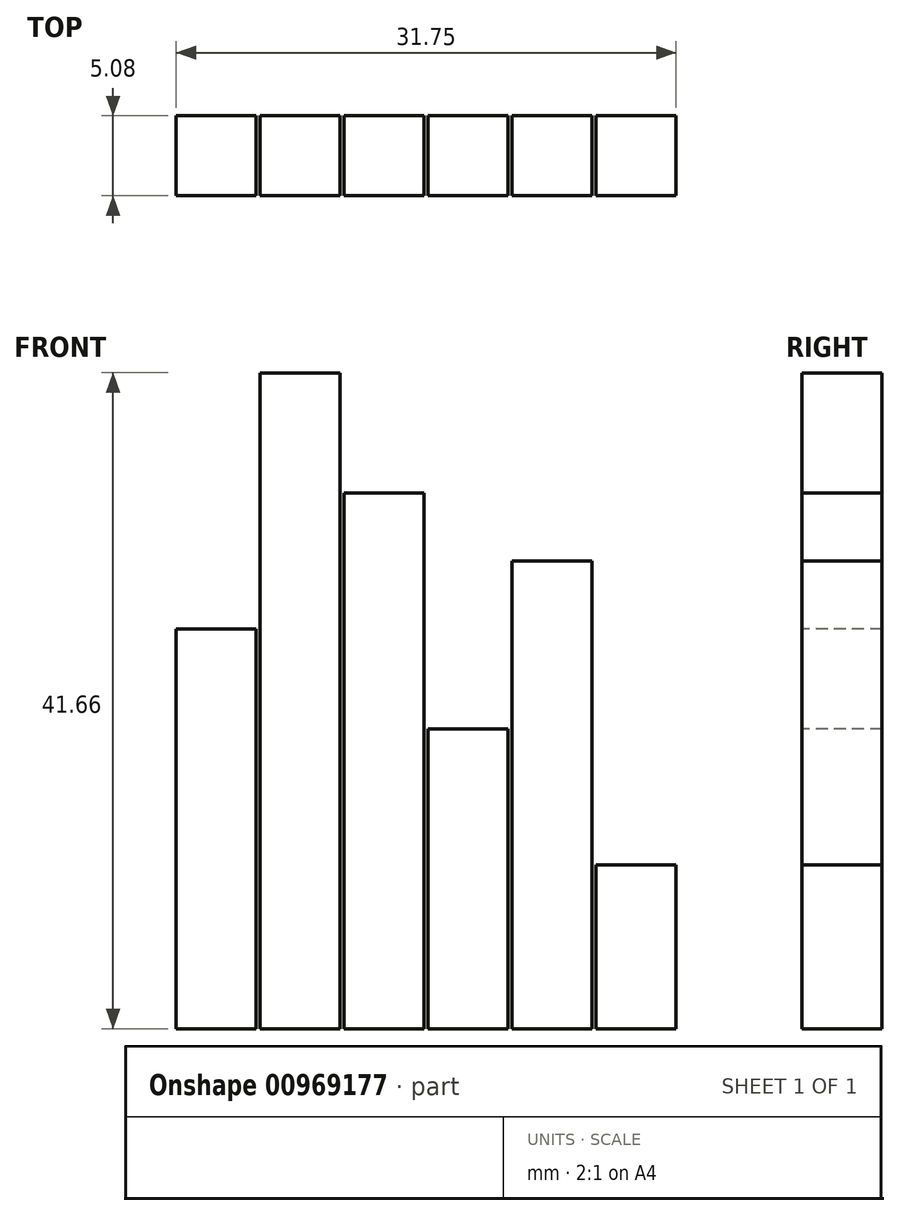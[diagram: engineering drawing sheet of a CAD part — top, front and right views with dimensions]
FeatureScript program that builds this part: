
annotation { "Feature Type Name" : "Feature", "Feature Type Description" : "" }
export const myFeature = defineFeature(function(context is Context, id is Id, definition is map)
    precondition{}
    {
        {
            var Q0;
            Q0=qCreatedBy(makeId("Top.planeOp"),FACE);
            var sketch = newSketch(context, id + "F0", { "sketchPlane" : qUnion([Q0])});
            skLineSegment(sketch, "E0.bottom", {"start": v(0, 0) * mm, "end": v(5.08, 0) * mm});
            skLineSegment(sketch, "E0.top", {"start": v(0, -5.08) * mm, "end": v(5.08, -5.08) * mm});
            skLineSegment(sketch, "E0.left", {"start": v(0, 0) * mm, "end": v(0, -5.08) * mm});
            skLineSegment(sketch, "E0.right", {"start": v(5.08, 0) * mm, "end": v(5.08, -5.08) * mm});
            skSolve(sketch);
        }
        {
            var Q0;
            Q0=qCreatedBy(makeId("Top.planeOp"),FACE);
            var sketch = newSketch(context, id + "F1", { "sketchPlane" : qUnion([Q0])});
            skLineSegment(sketch, "E1.0.0", {"start": v(0, 0) * mm, "end": v(0, -5.08) * mm});
            skLineSegment(sketch, "E1.0.1", {"start": v(0, -5.08) * mm, "end": v(5.08, -5.08) * mm});
            skLineSegment(sketch, "E1.0.2", {"start": v(5.08, -5.08) * mm, "end": v(5.08, 0) * mm});
            skLineSegment(sketch, "E1.0.3", {"start": v(5.08, 0) * mm, "end": v(0, 0) * mm});
            skLineSegment(sketch, "E2.1.0.0", {"start": v(10.41, 0) * mm, "end": v(5.33, 0) * mm});
            skLineSegment(sketch, "E2.1.0.1", {"start": v(5.33, -5.08) * mm, "end": v(10.41, -5.08) * mm});
            skLineSegment(sketch, "E2.1.0.2", {"start": v(5.33, 0) * mm, "end": v(5.33, -5.08) * mm});
            skLineSegment(sketch, "E2.1.0.3", {"start": v(10.41, -5.08) * mm, "end": v(10.41, 0) * mm});
            skLineSegment(sketch, "E2.2.0.0", {"start": v(15.75, 0) * mm, "end": v(10.67, 0) * mm});
            skLineSegment(sketch, "E2.2.0.1", {"start": v(10.67, -5.08) * mm, "end": v(15.75, -5.08) * mm});
            skLineSegment(sketch, "E2.2.0.2", {"start": v(10.67, 0) * mm, "end": v(10.67, -5.08) * mm});
            skLineSegment(sketch, "E2.2.0.3", {"start": v(15.75, -5.08) * mm, "end": v(15.75, 0) * mm});
            skLineSegment(sketch, "E2.3.0.0", {"start": v(21.08, 0) * mm, "end": v(16, 0) * mm});
            skLineSegment(sketch, "E2.3.0.1", {"start": v(16, -5.08) * mm, "end": v(21.08, -5.08) * mm});
            skLineSegment(sketch, "E2.3.0.2", {"start": v(16, 0) * mm, "end": v(16, -5.08) * mm});
            skLineSegment(sketch, "E2.3.0.3", {"start": v(21.08, -5.08) * mm, "end": v(21.08, 0) * mm});
            skLineSegment(sketch, "E2.direction1", {"start": v(0, -5.08) * mm, "end": v(5.33, -5.08) * mm, "construction": true});
            skLineSegment(sketch, "E3.0.4.0", {"start": v(26.42, 0) * mm, "end": v(21.34, 0) * mm});
            skLineSegment(sketch, "E3.3.4.0", {"start": v(21.34, -5.08) * mm, "end": v(26.42, -5.08) * mm});
            skLineSegment(sketch, "E3.6.4.0", {"start": v(21.34, 0) * mm, "end": v(21.34, -5.08) * mm});
            skLineSegment(sketch, "E3.9.4.0", {"start": v(26.42, -5.08) * mm, "end": v(26.42, 0) * mm});
            skLineSegment(sketch, "E3.0.5.0", {"start": v(31.75, 0) * mm, "end": v(26.67, 0) * mm});
            skLineSegment(sketch, "E3.3.5.0", {"start": v(26.67, -5.08) * mm, "end": v(31.75, -5.08) * mm});
            skLineSegment(sketch, "E3.6.5.0", {"start": v(26.67, 0) * mm, "end": v(26.67, -5.08) * mm});
            skLineSegment(sketch, "E3.9.5.0", {"start": v(31.75, -5.08) * mm, "end": v(31.75, 0) * mm});
            skSolve(sketch);
        }
        {
            var Q0;
            Q0=makeQuery(id+"F0.imprint","IMPRINT",FACE,{"disambiguationData":[TD([[makeQuery(id+"F0.imprint","IMPRINT",EDGE,{"derivedFrom":sQuery(id+"F0.wireOp",EDGE,"E0.bottom")}),-1.0]])]});
            extrude(context, id + "F2", {"entities" : qUnion([Q0]), "depth" : 25.4 * mm, "offsetDistance" : 25.4 * mm});
        }
        {
            var Q0;
            Q0=makeQuery(id+"F1.imprint","IMPRINT",FACE,{"disambiguationData":[TD([[makeQuery(id+"F1.imprint","IMPRINT",EDGE,{"derivedFrom":sQuery(id+"F1.wireOp",EDGE,"E2.1.0.0")}),1.0]])]});
            extrude(context, id + "F3", {"entities" : qUnion([Q0]), "depth" : 41.66 * mm, "offsetDistance" : 25.4 * mm});
        }
        {
            var Q0;
            Q0=makeQuery(id+"F1.imprint","IMPRINT",FACE,{"disambiguationData":[TD([[makeQuery(id+"F1.imprint","IMPRINT",EDGE,{"derivedFrom":sQuery(id+"F1.wireOp",EDGE,"E2.2.0.0")}),1.0]])]});
            extrude(context, id + "F4", {"entities" : qUnion([Q0]), "depth" : 34.04 * mm, "offsetDistance" : 25.4 * mm});
        }
        {
            var Q0;
            Q0=makeQuery(id+"F1.imprint","IMPRINT",FACE,{"disambiguationData":[TD([[makeQuery(id+"F1.imprint","IMPRINT",EDGE,{"derivedFrom":sQuery(id+"F1.wireOp",EDGE,"E2.3.0.0")}),1.0]])]});
            extrude(context, id + "F5", {"entities" : qUnion([Q0]), "depth" : 19.05 * mm, "offsetDistance" : 25.4 * mm});
        }
        {
            var Q0;
            Q0=makeQuery(id+"F1.imprint","IMPRINT",FACE,{"disambiguationData":[TD([[makeQuery(id+"F1.imprint","IMPRINT",EDGE,{"derivedFrom":sQuery(id+"F1.wireOp",EDGE,"E3.0.4.0")}),1.0]])]});
            extrude(context, id + "F6", {"entities" : qUnion([Q0]), "depth" : 29.72 * mm, "offsetDistance" : 25.4 * mm});
        }
        {
            var Q0;
            Q0=makeQuery(id+"F1.imprint","IMPRINT",FACE,{"disambiguationData":[TD([[makeQuery(id+"F1.imprint","IMPRINT",EDGE,{"derivedFrom":sQuery(id+"F1.wireOp",EDGE,"E3.0.5.0")}),1.0]])]});
            extrude(context, id + "F7", {"entities" : qUnion([Q0]), "depth" : 10.4 * mm, "offsetDistance" : 25.4 * mm});
        }
    });
